# Revit family: QF_RATIONAL_CombiSteamer_iCP_20-11G
name_source: partatom
category: Specialty Equipment
revit_build: Autodesk Revit 2018 (Build: 20170223_1515(x64)
units: mm (PartAtom-declared; Revit-internal decimal feet)

## family parameters
Always vertical = Yes
Cut with Voids When Loaded = No
OmniClass Number = 23.40.40.14.17.11
OmniClass Title = Cookers, Ovens, Stoves
Part Type = Normal
Room Calculation Point = No
Round Connector Dimension = Use Diameter
Shared = No
Work Plane-Based = No

## types (11) — shared parameters
Assembly Code = E1090320
Cold Water Flow = 0.2 L/s
Cold Water Maximum Pressure = 6.0 bar
Cold Water Minimum Pressure = 1.0 bar
Cold Water Size = 1"
Conn Conduit = No
Cycle = 50 Hz
Cycle Alternative = 60 Hz
Depth Actual = 848 mm  [stored 2.78215 ft]
Description = Gas Combi-steamer (20 x 2/1 GN / 40 x 1/1 GN)
Direct Waste Size = 2"
Fuel Type = G20,G25,G30,G31
G20 Gas Flow Max = 0.0
G20 Gas Flow Min = 0.0
G20 Gas kW = 42 kW
G25 Gas Flow Max = 0.0
G25 Gas Flow Min = 0.0
G25 Gas kW = 42 kW
G30 Gas Flow Max = 0.1
G30 Gas Flow Min = 0.0
G30 Gas kW = 42 kW
G31 Gas Flow Max = 0.1
G31 Gas Flow Min = 0.0
G31 Gas kW = 42 kW
Gas Size = 1"
Height Actual = 1807 mm
Latent Heat Output = 2 kW
Length Actual = 876 mm
Manufacturer = RATIONAL AG
Max Overcurrent Protection = 16 A
Model = iCombi Pro 20-1/1 G
Sensitive Heat Output = 2 kW
Sound Level = 60dBA
Specification by Manufacturer = Hot-air steamer (combi-steamer mode) for most of the cooking methods used in commercial kitchens for the optional use of steam and hot-air, individually, in succession or in combination.
URL = www.rational-online.com
Version = 05-2020
Warranty Duration = 2 years
Waste Water Discharge Temperature = 65 °C
Watts = 1300 W
Weight = 276.00 kg

## per-type parameters (varying)
| type | FL Amps | Phase | Volts |
| 20-1/1G 1NAC 100V | 13 A | 1 | 100 V |
| 20-1/1G 2AC 240V | 5 A | 2 | 240 V |
| 20-1/1G 2AC 230V | 6 A | 2 | 230 V |
| 20-1/1G 2AC 220V | 6 A | 2 | 220 V |
| 20-1/1G 2AC 208V | 6 A | 2 | 208 V |
| 20-1/1G 2AC 200V | 7 A | 2 | 200 V |
| 20-1/1G 1NAC 240V | 5 A | 1 | 240 V |
| 20-1/1G 1NAC 230V | 6 A | 1 | 230 V |
| 20-1/1G 1NAC 127V | 10 A | 1 | 127 V |
| 20-1/1G 1NAC 120V | 11 A | 1 | 120 V |
| 20-1/1G 1NAC 110V | 12 A | 1 | 110 V |

note: source unit labels omitted for G20 Gas Flow Max, G20 Gas Flow Min, G25 Gas Flow Max, G25 Gas Flow Min, G30 Gas Flow Max, G30 Gas Flow Min, G31 Gas Flow Max, G31 Gas Flow Min — the stored unit's dimension contradicts the parameter name (converter mislabeling)

note: [stored X ft] marks values corroborated as IEEE doubles in the binary element streams (Revit-internal decimal feet)

## geometry (parser evidence)
native form markers: Sweep x10
no freeform markers — native parametric forms only
